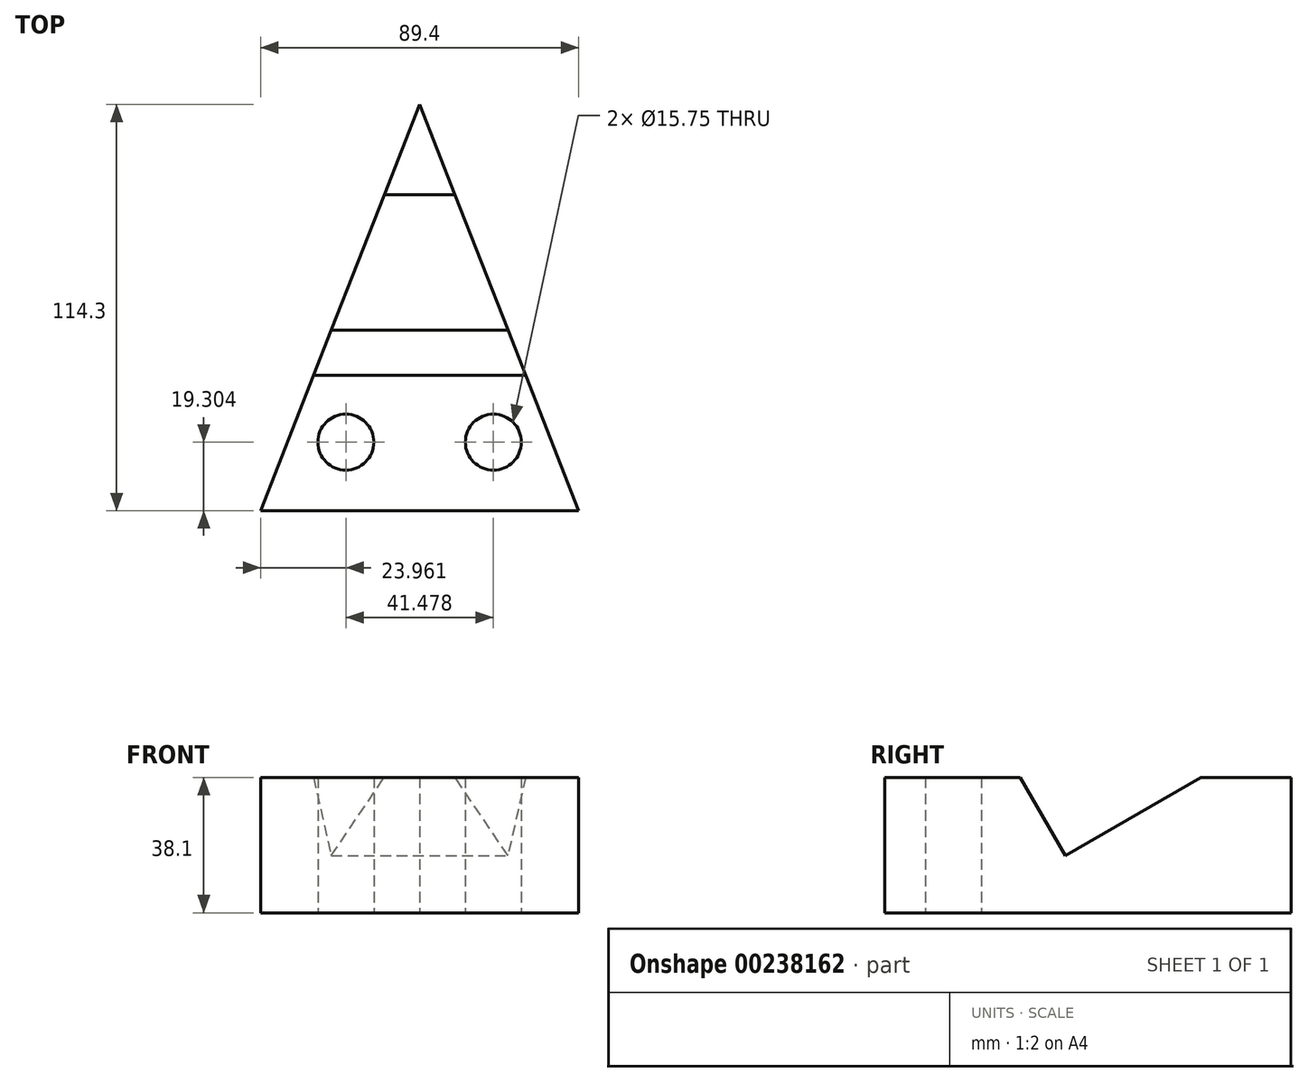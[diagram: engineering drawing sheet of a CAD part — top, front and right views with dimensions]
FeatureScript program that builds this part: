
annotation { "Feature Type Name" : "Feature", "Feature Type Description" : "" }
export const myFeature = defineFeature(function(context is Context, id is Id, definition is map)
    precondition{}
    {
        {
            var Q0;
            Q0=qCreatedBy(makeId("Top.planeOp"),FACE);
            var sketch = newSketch(context, id + "F0", { "sketchPlane" : qUnion([Q0])});
            skLineSegment(sketch, "E0", {"start": v(-44.7, -57.15) * mm, "end": v(44.7, -57.15) * mm});
            skLineSegment(sketch, "E1", {"start": v(-44.7, -57.15) * mm, "end": v(0, 57.15) * mm});
            skLineSegment(sketch, "E2", {"start": v(44.7, -57.15) * mm, "end": v(0, 57.15) * mm});
            skCircle(sketch, "E3", {"center": v(-20.74, -37.85) * mm, "radius": 7.87 * mm});
            skLineSegment(sketch, "E4", {"start": v(0, 57.15) * mm, "end": v(0, -57.15) * mm, "construction": true});
            skCircle(sketch, "E5.MirrorC", {"center": v(20.74, -37.85) * mm, "radius": 7.87 * mm});
            skSolve(sketch);
        }
        {
            var Q0;
            Q0 = qSketchRegion(id + "F0", true);
            extrude(context, id + "F1", {"entities" : qUnion([Q0]), "depth" : 38.1 * mm});
        }
        {
            var Q0;
            Q0=qCreatedBy(makeId("Right.planeOp"),FACE);
            cPlane(context, id + "F2", {"entities" : qUnion([Q0]), "cplaneType" : CPlaneType.OFFSET, "offset" : 44.7 * mm, "width" : 152.4 * mm, "height" : 152.4 * mm});
        }
        {
            var Q0;
            Q0=qCreatedBy(id+"F2.planeOp",FACE);
            var sketch = newSketch(context, id + "F3", { "sketchPlane" : qUnion([Q0])});
            skLineSegment(sketch, "E6", {"start": v(-19.05, 38.1) * mm, "end": v(31.75, 38.1) * mm});
            skLineSegment(sketch, "E7", {"start": v(31.75, 38.1) * mm, "end": v(-6.35, 16.1) * mm});
            skLineSegment(sketch, "E8", {"start": v(-6.35, 16.1) * mm, "end": v(-19.05, 38.1) * mm});
            skSolve(sketch);
        }
        {
            var Q0;
            Q0 = qSketchRegion(id + "F3", true);
            extrude(context, id + "F4", {"entities" : qUnion([Q0]), "operationType" : NewBodyOperationType.REMOVE, "oppositeDirection" : true, "depth" : 89.4 * mm});
        }
    });
